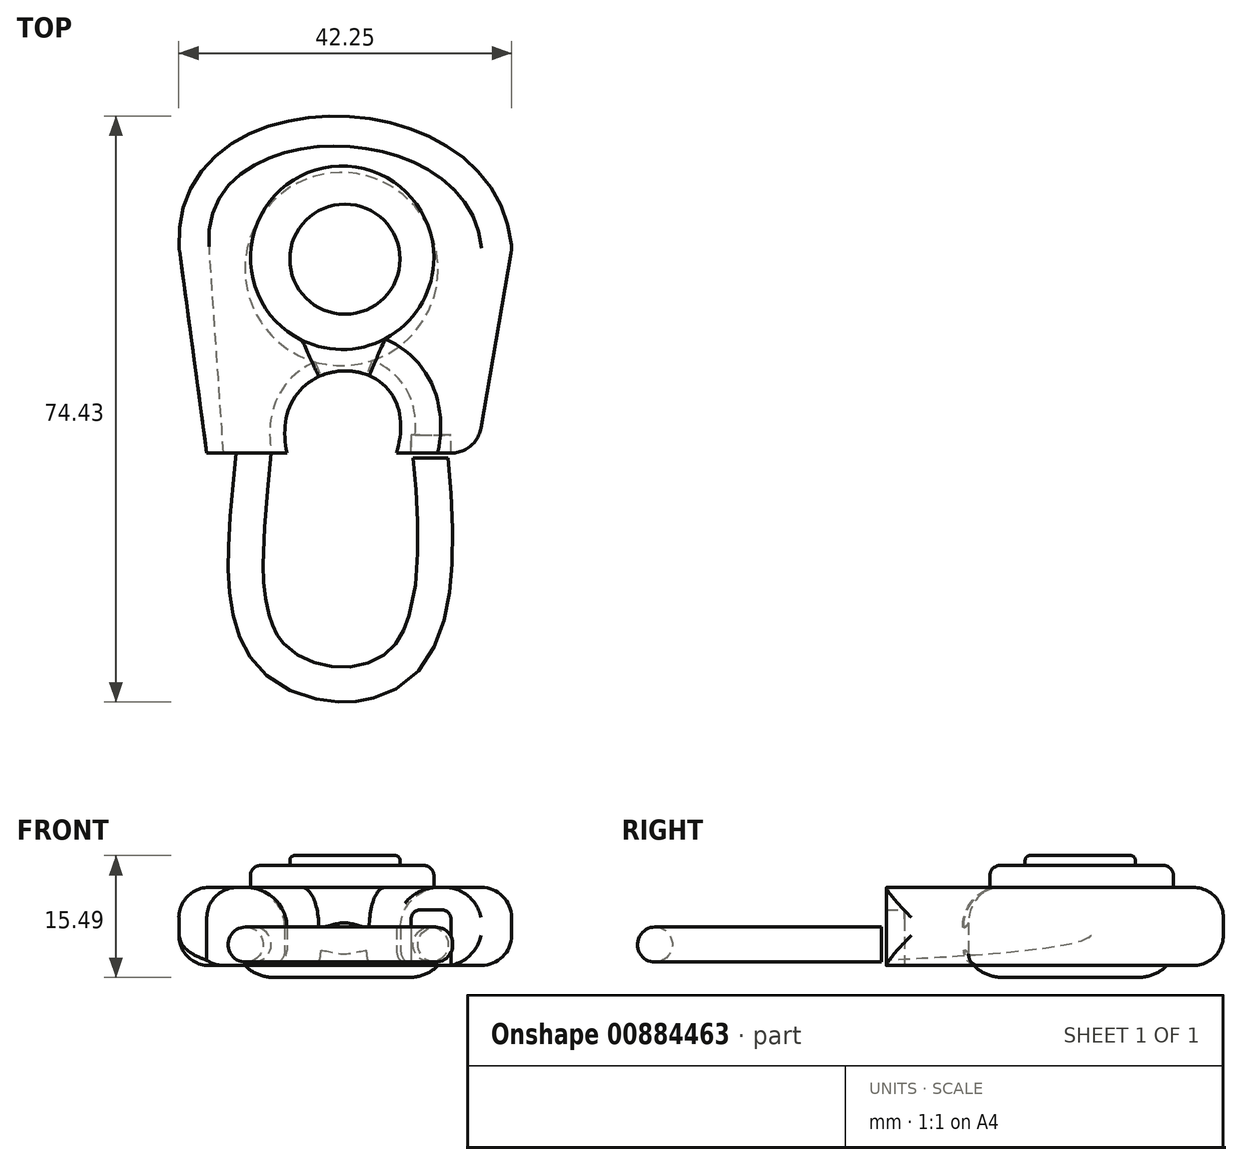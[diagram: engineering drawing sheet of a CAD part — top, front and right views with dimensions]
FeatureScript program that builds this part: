
annotation { "Feature Type Name" : "Feature", "Feature Type Description" : "" }
export const myFeature = defineFeature(function(context is Context, id is Id, definition is map)
    precondition{}
    {
        {
            var Q0;
            Q0=qCreatedBy(makeId("Front.planeOp"),FACE);
            var sketch = newSketch(context, id + "F0", { "sketchPlane" : qUnion([Q0])});
            skCircle(sketch, "E0", {"center": v(-66.96, 2.66) * mm, "radius": 2.23 * mm});
            skSolve(sketch);
        }
        {
            var Q0;
            Q0=qCreatedBy(makeId("Top.planeOp"),FACE);
            var sketch = newSketch(context, id + "F1", { "sketchPlane" : qUnion([Q0])});
            skFitSpline(sketch, "E1", {"points": [v(-66.54, 0) * mm, v(-64.57, -27.82) * mm, v(-49.62, -29.46) * mm, v(-45.44, 0) * mm], "startDerivative": vector(-8.66, -97.22) * mm, "endDerivative": vector(-12.67, 109.59) * mm});
            skSolve(sketch);
        }
        {
            var Q0;
            Q0=makeQuery(id+"F0.imprint","IMPRINT",FACE,{"disambiguationData":[TD([[makeQuery(id+"F0.imprint","IMPRINT",EDGE,{"derivedFrom":sQuery(id+"F0.wireOp",EDGE,"E0")}),1.0]])]});
            var Q1;
            Q1=sQuery(id+"F1.wireOp",EDGE,"E1");
            sweep(context, id + "F2", {"profiles" : qUnion([Q0]), "path" : qUnion([Q1])});
        }
        {
            var Q0;
            Q0=qCreatedBy(makeId("Top.planeOp"),FACE);
            var sketch = newSketch(context, id + "F3", { "sketchPlane" : qUnion([Q0])});
            skLineSegment(sketch, "E2", {"start": v(-49.04, -2.3) * mm, "end": v(-38.86, -2.3) * mm});
            skLineSegment(sketch, "E3", {"start": v(-38.86, -2.3) * mm, "end": v(-34.4, 23.58) * mm});
            skFitSpline(sketch, "E4", {"points": [v(-34.4, 23.58) * mm, v(-76.63, 23.58) * mm], "startDerivative": vector(-4.45, 66.92) * mm, "endDerivative": vector(4.82, -68.53) * mm});
            skLineSegment(sketch, "E5", {"start": v(-76.63, 23.58) * mm, "end": v(-73.13, -2.3) * mm});
            skLineSegment(sketch, "E6", {"start": v(-73.13, -2.3) * mm, "end": v(-62.96, -2.3) * mm});
            skFitSpline(sketch, "E7", {"points": [v(-62.96, -2.3) * mm, v(-49.04, -2.3) * mm], "startDerivative": vector(-8.57, 41.76) * mm, "endDerivative": vector(-12.31, -41.76) * mm});
            skSolve(sketch);
        }
        {
            var Q0;
            Q0=makeQuery(id+"F3.imprint","IMPRINT",FACE,{"disambiguationData":[TD([[makeQuery(id+"F3.imprint","IMPRINT",EDGE,{"derivedFrom":sQuery(id+"F3.wireOp",EDGE,"E2")}),1.0]])]});
            extrude(context, id + "F4", {"entities" : qUnion([Q0]), "operationType" : NewBodyOperationType.ADD, "depth" : 9.9 * mm, "offsetDistance" : 25.4 * mm});
        }
        {
            var Q0;
            Q0=makeQuery(id+"F4.opExtrude","SWEPT_FACE",FACE,{"disambiguationData":[OSD([sQuery(id+"F3.wireOp",EDGE,"E4")])]});
            var Q1;
            Q1=makeQuery(id+"F4.opExtrude","CAP_EDGE",EDGE,{"disambiguationData":[OSD([sQuery(id+"F3.wireOp",EDGE,"E5")])],"isStart":false});
            var Q2;
            Q2=makeQuery(id+"F4.opExtrude","SWEPT_FACE",FACE,{"disambiguationData":[OSD([sQuery(id+"F3.wireOp",EDGE,"E3")])]});
            fillet(context, id + "F5", {"entities" : qUnion([Q0, Q1, Q2]), "radius" : 3.8 * mm, "tangentPropagation" : true, "allowEdgeOverflow" : false});
        }
        {
            var Q0;
            Q0=qCreatedBy(makeId("Top.planeOp"),FACE);
            var sketch = newSketch(context, id + "F6", { "sketchPlane" : qUnion([Q0])});
            skCircle(sketch, "E8", {"center": v(-55.94, 22.5) * mm, "radius": 11.65 * mm});
            skSolve(sketch);
        }
        {
            var Q0;
            Q0=makeQuery(id+"F6.imprint","IMPRINT",FACE,{"disambiguationData":[TD([[makeQuery(id+"F6.imprint","IMPRINT",EDGE,{"derivedFrom":sQuery(id+"F6.wireOp",EDGE,"E8")}),1.0]])]});
            extrude(context, id + "F7", {"entities" : qUnion([Q0]), "operationType" : NewBodyOperationType.ADD, "depth" : 12.7 * mm, "offsetDistance" : 25.4 * mm});
        }
        {
            var Q0;
            Q0=makeQuery(id+"F7.opExtrude","CAP_EDGE",EDGE,{"disambiguationData":[OSD([sQuery(id+"F6.wireOp",EDGE,"E8")])],"isStart":false});
            fillet(context, id + "F8", {"entities" : qUnion([Q0]), "radius" : 1.27 * mm, "tangentPropagation" : true, "allowEdgeOverflow" : false});
        }
        {
            var Q0;
            Q0=qCreatedBy(makeId("Top.planeOp"),FACE);
            var sketch = newSketch(context, id + "F9", { "sketchPlane" : qUnion([Q0])});
            skCircle(sketch, "E9", {"center": v(-55.59, 22.33) * mm, "radius": 7 * mm});
            skSolve(sketch);
        }
        {
            var Q0;
            Q0=makeQuery(id+"F9.imprint","IMPRINT",FACE,{"disambiguationData":[TD([[makeQuery(id+"F9.imprint","IMPRINT",EDGE,{"derivedFrom":sQuery(id+"F9.wireOp",EDGE,"E9")}),1.0]])]});
            extrude(context, id + "F10", {"entities" : qUnion([Q0]), "operationType" : NewBodyOperationType.ADD, "depth" : 13.97 * mm, "offsetDistance" : 25.4 * mm});
        }
        {
            var Q0;
            Q0=makeQuery(id+"F10.opExtrude","CAP_EDGE",EDGE,{"disambiguationData":[OSD([sQuery(id+"F9.wireOp",EDGE,"E9")])],"isStart":false});
            fillet(context, id + "F11", {"entities" : qUnion([Q0]), "radius" : 0.61 * mm, "tangentPropagation" : true, "allowEdgeOverflow" : false});
        }
        {
            var Q0;
            Q0=qCreatedBy(makeId("Top.planeOp"),FACE);
            var sketch = newSketch(context, id + "F12", { "sketchPlane" : qUnion([Q0])});
            skCircle(sketch, "E10", {"center": v(-56.02, 21.08) * mm, "radius": 12.27 * mm});
            skSolve(sketch);
        }
        {
            var Q0;
            Q0 = qSketchRegion(id + "F12", true);
            extrude(context, id + "F13", {"entities" : qUnion([Q0]), "operationType" : NewBodyOperationType.ADD, "oppositeDirection" : true, "depth" : 1.52 * mm, "offsetDistance" : 25.4 * mm});
        }
        {
            var Q0;
            Q0=makeQuery(id+"F13.opExtrude","CAP_EDGE",EDGE,{"disambiguationData":[OSD([sQuery(id+"F12.wireOp",EDGE,"E10")])],"isStart":false});
            var Q1;
            Q1=makeQuery(id+"F13.opExtrude","CAP_FACE",FACE,{"disambiguationData":[OSD([sQuery(id+"F12.wireOp",EDGE,"E10")])],"isStart":false});
            fillet(context, id + "F14", {"entities" : qUnion([Q0, Q1]), "radius" : 5.08 * mm, "tangentPropagation" : true, "allowEdgeOverflow" : false});
        }
        {
            var Q0;
            Q0=makeQuery(id+"F4.opExtrude","CAP_EDGE",EDGE,{"disambiguationData":[OSD([sQuery(id+"F3.wireOp",EDGE,"E7")])],"isStart":false});
            fillet(context, id + "F15", {"entities" : qUnion([Q0]), "radius" : 5.08 * mm, "tangentPropagation" : true, "allowEdgeOverflow" : false});
        }
        {
            var Q0;
            Q0=makeQuery(id+"F4.opExtrude","CAP_EDGE",EDGE,{"disambiguationData":[OSD([sQuery(id+"F3.wireOp",EDGE,"E7")])],"isStart":true});
            fillet(context, id + "F16", {"entities" : qUnion([Q0]), "radius" : 1.9 * mm, "tangentPropagation" : true, "allowEdgeOverflow" : false});
        }
        {
            var Q0;
            Q0=qCreatedBy(makeId("Front.planeOp"),FACE);
            var sketch = newSketch(context, id + "F17", { "sketchPlane" : qUnion([Q0])});
            skLineSegment(sketch, "E11.bottom", {"start": v(-47.17, 7.05) * mm, "end": v(-42.13, 7.05) * mm});
            skLineSegment(sketch, "E11.top", {"start": v(-47.17, -0.44) * mm, "end": v(-42.13, -0.44) * mm});
            skLineSegment(sketch, "E11.left", {"start": v(-47.17, 7.05) * mm, "end": v(-47.17, -0.44) * mm});
            skLineSegment(sketch, "E11.right", {"start": v(-42.13, 7.05) * mm, "end": v(-42.13, -0.44) * mm});
            skSolve(sketch);
        }
        {
            var Q0;
            Q0=makeQuery(id+"F17.imprint","IMPRINT",FACE,{"disambiguationData":[TD([[makeQuery(id+"F17.imprint","IMPRINT",EDGE,{"derivedFrom":sQuery(id+"F17.wireOp",EDGE,"E11.bottom")}),-1.0]])]});
            extrude(context, id + "F18", {"entities" : qUnion([Q0]), "operationType" : NewBodyOperationType.REMOVE, "depth" : 2.95 * mm, "offsetDistance" : 25.4 * mm});
        }
        {
            var Q0;
            Q0=makeQuery(id+"F18.boolean.opBoolean","COPY",EDGE,{"derivedFrom":makeQuery(id+"F18.opExtrude","SWEPT_EDGE",EDGE,{"disambiguationData":[OSD([sQuery(id+"F17.wireOp",EDGE,"E11.bottom"),sQuery(id+"F17.wireOp",EDGE,"E11.left")])]})});
            fillet(context, id + "F19", {"entities" : qUnion([Q0]), "radius" : 1.14 * mm, "tangentPropagation" : true, "allowEdgeOverflow" : false});
        }
        {
            var Q0;
            Q0=makeQuery(id+"F18.boolean.opBoolean","COPY",EDGE,{"derivedFrom":makeQuery(id+"F18.opExtrude","SWEPT_EDGE",EDGE,{"disambiguationData":[OSD([sQuery(id+"F17.wireOp",EDGE,"E11.bottom"),sQuery(id+"F17.wireOp",EDGE,"E11.right")])]})});
            fillet(context, id + "F20", {"entities" : qUnion([Q0]), "radius" : 1.14 * mm, "tangentPropagation" : true, "allowEdgeOverflow" : false});
        }
    });
